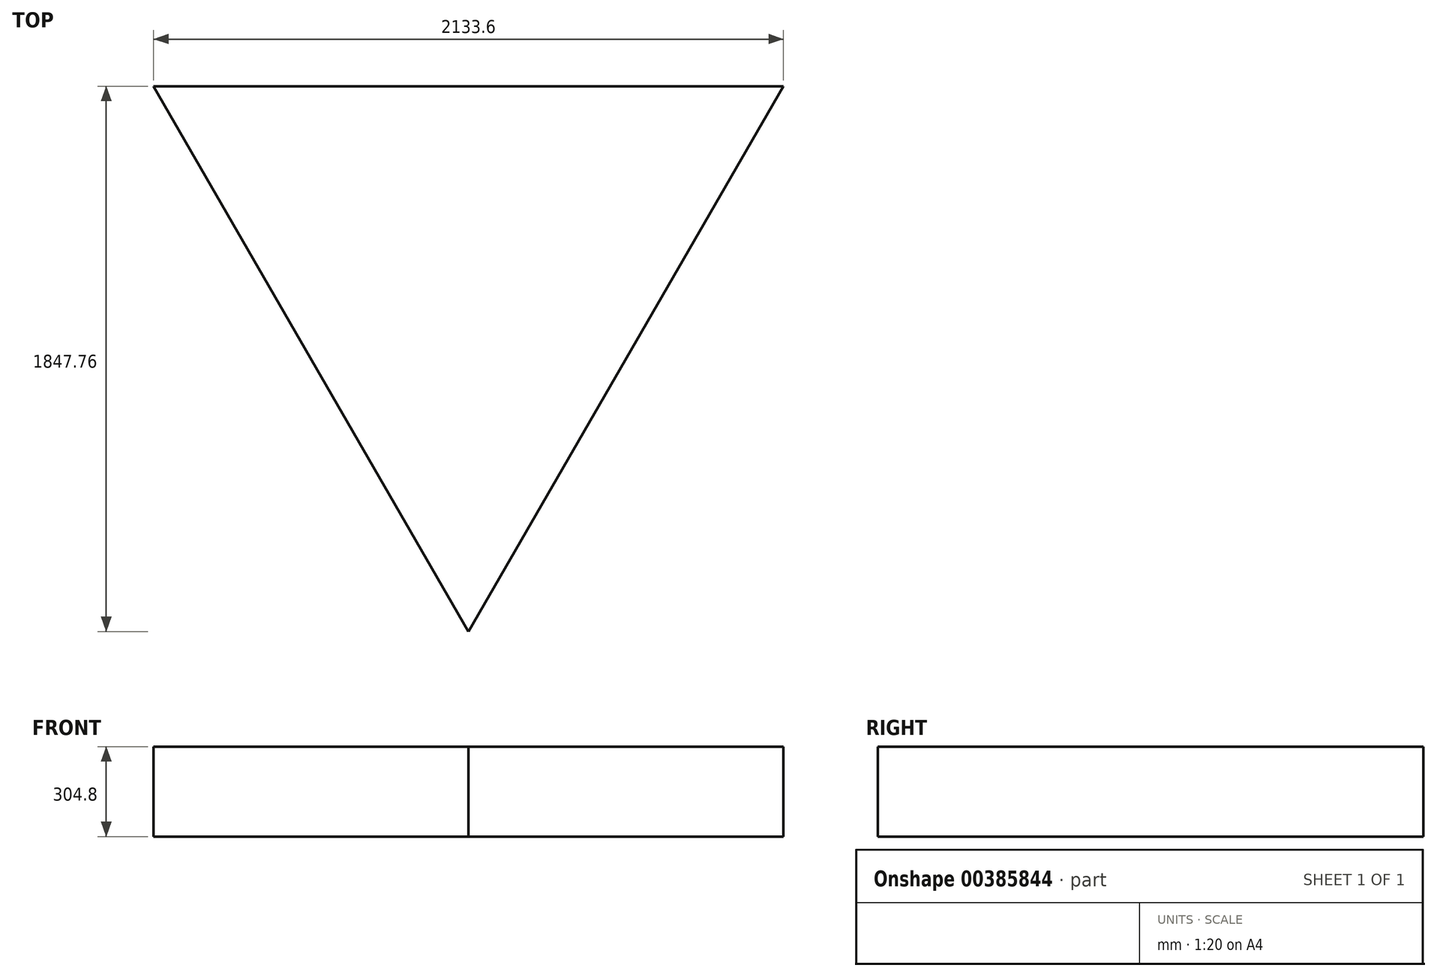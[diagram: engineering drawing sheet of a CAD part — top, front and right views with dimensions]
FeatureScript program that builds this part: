
annotation { "Feature Type Name" : "Feature", "Feature Type Description" : "" }
export const myFeature = defineFeature(function(context is Context, id is Id, definition is map)
    precondition{}
    {
        {
            var Q0;
            Q0=qCreatedBy(makeId("Top.planeOp"),FACE);
            var sketch = newSketch(context, id + "F0", { "sketchPlane" : qUnion([Q0])});
            skLineSegment(sketch, "E0", {"start": v(-1066.8, 1940.09) * mm, "end": v(1066.8, 1940.09) * mm});
            skLineSegment(sketch, "E1", {"start": v(1066.8, 1940.09) * mm, "end": v(0, 92.33) * mm});
            skLineSegment(sketch, "E2", {"start": v(0, 92.33) * mm, "end": v(-1066.8, 1940.09) * mm});
            skSolve(sketch);
        }
        {
            var Q0;
            Q0 = qSketchRegion(id + "F0", true);
            extrude(context, id + "F1", {"entities" : qUnion([Q0]), "depth" : 304.8 * mm});
        }
    });
